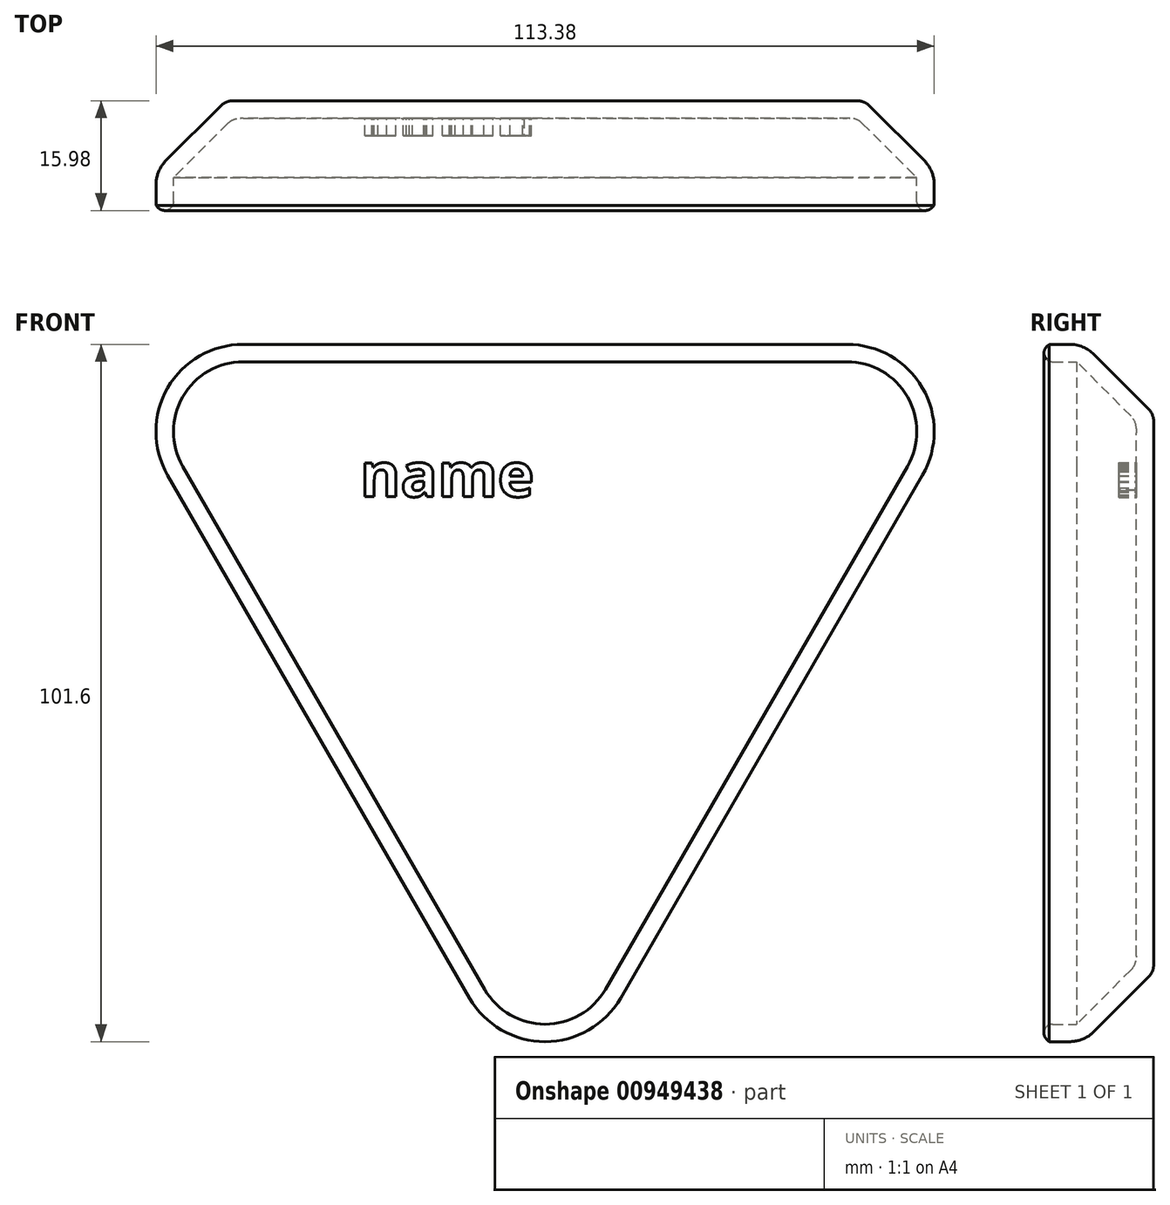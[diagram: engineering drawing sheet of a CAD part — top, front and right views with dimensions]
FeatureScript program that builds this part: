
annotation { "Feature Type Name" : "Feature", "Feature Type Description" : "" }
export const myFeature = defineFeature(function(context is Context, id is Id, definition is map)
    precondition{}
    {
        {
            var Q0;
            Q0=qCreatedBy(makeId("Front.planeOp"),FACE);
            var sketch = newSketch(context, id + "F0", { "sketchPlane" : qUnion([Q0])});
            skCircle(sketch, "E0.cCircle", {"center": v(0, 0) * mm, "radius": 38.1 * mm, "construction": true});
            skLineSegment(sketch, "E0.0", {"start": v(-44, 38.1) * mm, "end": v(44, 38.1) * mm});
            skLineSegment(sketch, "E0.1", {"start": v(55, 19.05) * mm, "end": v(11, -57.15) * mm});
            skLineSegment(sketch, "E0.2", {"start": v(-11, -57.15) * mm, "end": v(-55, 19.05) * mm});
            skPoint(sketch, "E0.0.midPoint", {"position": v(0, 38.1) * mm});
            skPoint(sketch, "E1.visualSharp", {"position": v(-66, 38.1) * mm});
            skArc(sketch, "E1.filletArc", {"start": v(-44, 38.1) * mm, "mid": v(-55, 31.75) * mm, "end": v(-55, 19.05) * mm});
            skPoint(sketch, "E2.visualSharp", {"position": v(66, 38.1) * mm});
            skArc(sketch, "E2.filletArc", {"start": v(55, 19.05) * mm, "mid": v(55, 31.75) * mm, "end": v(44, 38.1) * mm});
            skPoint(sketch, "E3.visualSharp", {"position": v(0, -76.2) * mm});
            skArc(sketch, "E3.filletArc", {"start": v(-11, -57.15) * mm, "mid": v(0, -63.5) * mm, "end": v(11, -57.15) * mm});
            skSolve(sketch);
        }
        {
            var Q0;
            Q0 = qSketchRegion(id + "F0", true);
            extrude(context, id + "F1", {"entities" : qUnion([Q0]), "endBound" : BoundingType.SYMMETRIC, "depth" : 25.4 * mm, "offsetDistance" : 25.4 * mm});
        }
        {
            var Q0;
            Q0=makeQuery(id+"F1.opExtrude","CAP_EDGE",EDGE,{"disambiguationData":[OSD([sQuery(id+"F0.wireOp",EDGE,"E2.filletArc")])],"isStart":false});
            var Q1;
            Q1=makeQuery(id+"F1.opExtrude","CAP_EDGE",EDGE,{"disambiguationData":[OSD([sQuery(id+"F0.wireOp",EDGE,"E2.filletArc")])],"isStart":true});
            chamfer(context, id + "F2", {"entities" : qUnion([Q0, Q1]), "width" : 10.16 * mm, "tangentPropagation" : true});
        }
        {
            var Q0;
            {var subQ0=sQuery(id+"F0.wireOp",EDGE,"E0.0");Q0=makeQuery(id+"F2.opChamfer","BLEND_FACE",FACE,{"disambiguationData":[OSD([subQ0]),TDD([makeQuery(id+"F1.opExtrude","CAP_EDGE",EDGE,{"disambiguationData":[OSD([subQ0])],"isStart":false})])]});}
            var Q1;
            {var subQ0=sQuery(id+"F0.wireOp",EDGE,"E1.filletArc");Q1=makeQuery(id+"F2.opChamfer","BLEND_FACE",FACE,{"disambiguationData":[OSD([subQ0]),TDD([makeQuery(id+"F1.opExtrude","CAP_EDGE",EDGE,{"disambiguationData":[OSD([subQ0])],"isStart":false})])]});}
            var Q2;
            Q2=makeQuery(id+"F1.opExtrude","CAP_FACE",FACE,{"disambiguationData":[OSD([sQuery(id+"F0.wireOp",EDGE,"E0.0"),sQuery(id+"F0.wireOp",EDGE,"E0.1"),sQuery(id+"F0.wireOp",EDGE,"E0.2"),sQuery(id+"F0.wireOp",EDGE,"E1.filletArc"),sQuery(id+"F0.wireOp",EDGE,"E2.filletArc"),sQuery(id+"F0.wireOp",EDGE,"E3.filletArc")])],"isStart":false});
            var Q3;
            {var subQ0=sQuery(id+"F0.wireOp",EDGE,"E0.2");Q3=makeQuery(id+"F2.opChamfer","BLEND_FACE",FACE,{"disambiguationData":[OSD([subQ0]),TDD([makeQuery(id+"F1.opExtrude","CAP_EDGE",EDGE,{"disambiguationData":[OSD([subQ0])],"isStart":false})])]});}
            var Q4;
            {var subQ0=sQuery(id+"F0.wireOp",EDGE,"E3.filletArc");Q4=makeQuery(id+"F2.opChamfer","BLEND_FACE",FACE,{"disambiguationData":[OSD([subQ0]),TDD([makeQuery(id+"F1.opExtrude","CAP_EDGE",EDGE,{"disambiguationData":[OSD([subQ0])],"isStart":false})])]});}
            var Q5;
            {var subQ0=sQuery(id+"F0.wireOp",EDGE,"E0.1");Q5=makeQuery(id+"F2.opChamfer","BLEND_FACE",FACE,{"disambiguationData":[OSD([subQ0]),TDD([makeQuery(id+"F1.opExtrude","CAP_EDGE",EDGE,{"disambiguationData":[OSD([subQ0])],"isStart":false})])]});}
            var Q6;
            {var subQ0=sQuery(id+"F0.wireOp",EDGE,"E2.filletArc");Q6=makeQuery(id+"F2.opChamfer","BLEND_FACE",FACE,{"disambiguationData":[OSD([subQ0]),TDD([makeQuery(id+"F1.opExtrude","CAP_EDGE",EDGE,{"disambiguationData":[OSD([subQ0])],"isStart":false})])]});}
            shell(context, id + "F3", {"entities" : qUnion([Q0, Q1, Q2, Q3, Q4, Q5, Q6]), "thickness" : 2.54 * mm});
        }
        {
            var Q0;
            {var subQ0=sQuery(id+"F0.wireOp",EDGE,"E1.filletArc");Q0=makeQuery(id+"F3.opShell","OFFSET_EDGE",EDGE,{"disambiguationData":[OSD([subQ0]),TDD([makeQuery(id+"F2.opChamfer","BLEND_EDGE",EDGE,{"blendedFrom":[makeQuery(id+"F1.opExtrude","CAP_EDGE",EDGE,{"disambiguationData":[OSD([subQ0])],"isStart":false}),makeQuery(id+"F1.opExtrude","SWEPT_FACE",FACE,{"disambiguationData":[OSD([subQ0])]})],"blendedInto":[makeQuery(id+"F1.opExtrude","SWEPT_FACE",FACE,{"disambiguationData":[OSD([subQ0])]})]})])]});}
            fillet(context, id + "F4", {"entities" : qUnion([Q0]), "radius" : 1.27 * mm, "tangentPropagation" : true, "allowEdgeOverflow" : false});
        }
        {
            var Q0;
            {var subQ0=sQuery(id+"F0.wireOp",EDGE,"E0.2");Q0=makeQuery(id+"F2.opChamfer","BLEND_EDGE",EDGE,{"blendedFrom":[makeQuery(id+"F1.opExtrude","CAP_EDGE",EDGE,{"disambiguationData":[OSD([subQ0])],"isStart":true}),makeQuery(id+"F1.opExtrude","CAP_FACE",FACE,{"disambiguationData":[OSD([sQuery(id+"F0.wireOp",EDGE,"E0.0"),sQuery(id+"F0.wireOp",EDGE,"E0.1"),subQ0,sQuery(id+"F0.wireOp",EDGE,"E1.filletArc"),sQuery(id+"F0.wireOp",EDGE,"E2.filletArc"),sQuery(id+"F0.wireOp",EDGE,"E3.filletArc")])],"isStart":true})],"blendedInto":[makeQuery(id+"F1.opExtrude","CAP_FACE",FACE,{"disambiguationData":[OSD([sQuery(id+"F0.wireOp",EDGE,"E0.0"),sQuery(id+"F0.wireOp",EDGE,"E0.1"),subQ0,sQuery(id+"F0.wireOp",EDGE,"E1.filletArc"),sQuery(id+"F0.wireOp",EDGE,"E2.filletArc"),sQuery(id+"F0.wireOp",EDGE,"E3.filletArc")])],"isStart":true})]});}
            var Q1;
            {var subQ0=sQuery(id+"F0.wireOp",EDGE,"E3.filletArc");var subQ1=sQuery(id+"F0.wireOp",EDGE,"E2.filletArc");var subQ2=sQuery(id+"F0.wireOp",EDGE,"E1.filletArc");var subQ3=sQuery(id+"F0.wireOp",EDGE,"E0.2");var subQ4=sQuery(id+"F0.wireOp",EDGE,"E0.1");var subQ5=sQuery(id+"F0.wireOp",EDGE,"E0.0");Q1=makeQuery(id+"F3.opShell","OFFSET_EDGE",EDGE,{"disambiguationData":[OSD([subQ5,subQ4,subQ3,subQ2,subQ1,subQ0]),TDD([makeQuery(id+"F2.opChamfer","BLEND_EDGE",EDGE,{"blendedFrom":[makeQuery(id+"F1.opExtrude","CAP_EDGE",EDGE,{"disambiguationData":[OSD([subQ5])],"isStart":true}),makeQuery(id+"F1.opExtrude","CAP_FACE",FACE,{"disambiguationData":[OSD([subQ5,subQ4,subQ3,subQ2,subQ1,subQ0])],"isStart":true})],"blendedInto":[makeQuery(id+"F1.opExtrude","CAP_FACE",FACE,{"disambiguationData":[OSD([subQ5,subQ4,subQ3,subQ2,subQ1,subQ0])],"isStart":true})]})])]});}
            fillet(context, id + "F5", {"entities" : qUnion([Q0, Q1]), "radius" : 2.54 * mm, "tangentPropagation" : true, "allowEdgeOverflow" : false});
        }
        {
            var Q0;
            {var subQ0=sQuery(id+"F0.wireOp",EDGE,"E0.2");Q0=makeQuery(id+"F2.opChamfer","BLEND_EDGE",EDGE,{"blendedFrom":[makeQuery(id+"F1.opExtrude","CAP_EDGE",EDGE,{"disambiguationData":[OSD([subQ0])],"isStart":true}),makeQuery(id+"F1.opExtrude","SWEPT_FACE",FACE,{"disambiguationData":[OSD([subQ0])]})],"blendedInto":[makeQuery(id+"F1.opExtrude","SWEPT_FACE",FACE,{"disambiguationData":[OSD([subQ0])]})]});}
            fillet(context, id + "F6", {"entities" : qUnion([Q0]), "radius" : 5.08 * mm, "tangentPropagation" : true, "allowEdgeOverflow" : false});
        }
        {
            var Q0;
            Q0=makeQuery(id+"F3.opShell","OFFSET_FACE",FACE,{"disambiguationData":[OSD([sQuery(id+"F0.wireOp",EDGE,"E0.0"),sQuery(id+"F0.wireOp",EDGE,"E0.1"),sQuery(id+"F0.wireOp",EDGE,"E0.2"),sQuery(id+"F0.wireOp",EDGE,"E1.filletArc"),sQuery(id+"F0.wireOp",EDGE,"E2.filletArc"),sQuery(id+"F0.wireOp",EDGE,"E3.filletArc")])]});
            var sketch = newSketch(context, id + "F7", { "sketchPlane" : qUnion([Q0])});
            skText(sketch, "E4", { "text": "name", "fontName": "OpenSans-Bold.ttf"});
            const initialGuessF7  = {"E4": [-0.02692, 0.0159, 1, 0, 0.00643]};
            skSetInitialGuess(sketch, initialGuessF7);
            skSolve(sketch);
        }
        {
            var Q0;
            Q0 = qSketchRegion(id + "F7", true);
            extrude(context, id + "F8", {"entities" : qUnion([Q0]), "operationType" : NewBodyOperationType.ADD, "depth" : 2.54 * mm, "offsetDistance" : 25.4 * mm});
        }
    });
